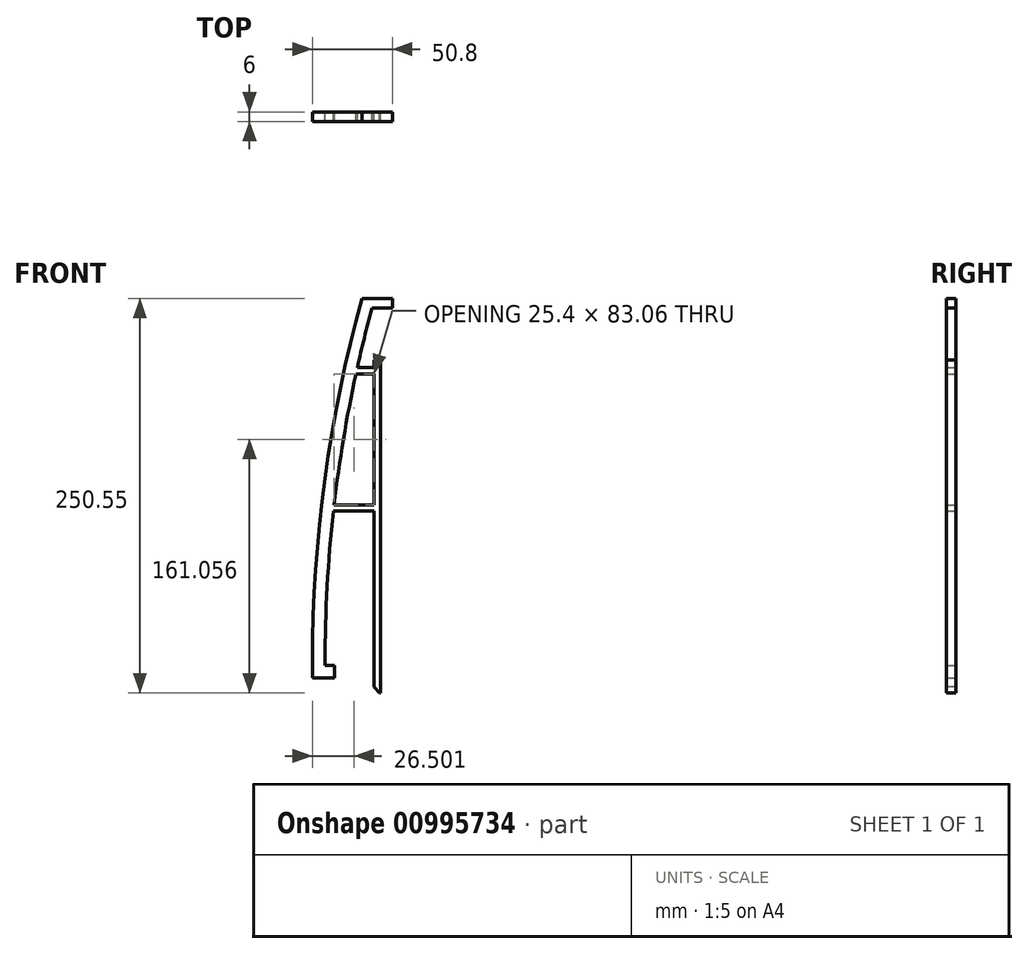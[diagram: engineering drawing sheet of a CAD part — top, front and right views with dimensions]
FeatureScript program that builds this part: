
annotation { "Feature Type Name" : "Feature", "Feature Type Description" : "" }
export const myFeature = defineFeature(function(context is Context, id is Id, definition is map)
    precondition{}
    {
        {
            var Q0;
            Q0=qCreatedBy(makeId("Front.planeOp"),FACE);
            var sketch = newSketch(context, id + "F0", { "sketchPlane" : qUnion([Q0])});
            skLineSegment(sketch, "E0", {"start": v(-4.2, 235) * mm, "end": v(-17.2, 235) * mm});
            skLineSegment(sketch, "E1", {"start": v(-4.2, 241) * mm, "end": v(-23.56, 241) * mm});
            skLineSegment(sketch, "E2", {"start": v(-47, 0) * mm, "end": v(-47, 10) * mm});
            skLineSegment(sketch, "E3", {"start": v(-55, 0) * mm, "end": v(-55, 10) * mm});
            skLineSegment(sketch, "E4", {"start": v(-47, 0) * mm, "end": v(-55, 0) * mm});
            skArc(sketch, "E5", {"start": v(-17.2, 235) * mm, "mid": v(-22.07, 216.07) * mm, "end": v(-26.52, 197.04) * mm});
            skArc(sketch, "E6", {"start": v(-23.56, 241) * mm, "mid": v(-47.1, 126.56) * mm, "end": v(-55, 10) * mm});
            skLineSegment(sketch, "E7", {"start": v(-4.2, 241) * mm, "end": v(-4.2, 235) * mm});
            skLineSegment(sketch, "E8", {"start": v(-11.8, -9.55) * mm, "end": v(-11.8, 197.04) * mm});
            skLineSegment(sketch, "E9", {"start": v(-15.8, 197.04) * mm, "end": v(-26.52, 197.04) * mm});
            skLineSegment(sketch, "E10", {"start": v(-27.4, 193.04) * mm, "end": v(-15.8, 193.04) * mm});
            skLineSegment(sketch, "E11", {"start": v(-15.8, 193.04) * mm, "end": v(-15.8, 109.97) * mm});
            skLineSegment(sketch, "E12", {"start": v(-15.8, -9.55) * mm, "end": v(-11.8, -9.55) * mm});
            skLineSegment(sketch, "E13", {"start": v(-15.8, 109.97) * mm, "end": v(-41.2, 109.97) * mm});
            skLineSegment(sketch, "E14", {"start": v(-15.8, 105.97) * mm, "end": v(-41.65, 105.97) * mm});
            skLineSegment(sketch, "E15", {"start": v(-15.8, 197.04) * mm, "end": v(-15.8, 202.04) * mm});
            skLineSegment(sketch, "E16", {"start": v(-15.8, 202.04) * mm, "end": v(-11.8, 202.04) * mm});
            skLineSegment(sketch, "E17", {"start": v(-11.8, 202.04) * mm, "end": v(-11.8, 197.04) * mm});
            skArc(sketch, "E18.trimOffspring", {"start": v(-27.4, 193.04) * mm, "mid": v(-35.3, 151.67) * mm, "end": v(-41.2, 109.97) * mm});
            skLineSegment(sketch, "E19.trimOffspring", {"start": v(-15.8, 105.97) * mm, "end": v(-15.8, -9.55) * mm});
            skArc(sketch, "E20.trimOffspring", {"start": v(-41.65, 105.97) * mm, "mid": v(-45.66, 58.06) * mm, "end": v(-47, 10) * mm});
            skSolve(sketch);
        }
        {
            var Q0;
            Q0=makeQuery(id+"F0.imprint","IMPRINT",FACE,{"disambiguationData":[TD([[makeQuery(id+"F0.imprint","IMPRINT",EDGE,{"derivedFrom":sQuery(id+"F0.wireOp",EDGE,"E0")}),-1.0]])]});
            extrude(context, id + "F1", {"entities" : qUnion([Q0]), "depth" : 6 * mm, "offsetDistance" : 25 * mm});
        }
        {
            var Q0;
            Q0=makeQuery(id+"F1.opExtrude","SWEPT_EDGE",EDGE,{"disambiguationData":[OSD([sQuery(id+"F0.wireOp",EDGE,"E12"),sQuery(id+"F0.wireOp",EDGE,"E19.trimOffspring")])]});
            chamfer(context, id + "F2", {"entities" : qUnion([Q0]), "chamferType" : ChamferType.TWO_OFFSETS, "width1" : 3.5 * mm, "oppositeDirection" : false, "width2" : 4 * mm, "tangentPropagation" : true});
        }
        {
            var Q0;
            Q0=makeQuery(id+"F1.opExtrude","SWEPT_FACE",FACE,{"disambiguationData":[OSD([sQuery(id+"F0.wireOp",EDGE,"E2")])]});
            extrude(context, id + "F3", {"entities" : qUnion([Q0]), "operationType" : NewBodyOperationType.ADD, "depth" : 6 * mm, "offsetDistance" : 25 * mm});
        }
        {
            var Q0;
            Q0=makeQuery(id+"F3.opExtrude","SWEPT_FACE",FACE,{"disambiguationData":[OSD([sQuery(id+"F0.wireOp",EDGE,"E2"),sQuery(id+"F0.wireOp",EDGE,"E20.trimOffspring")])]});
            extrude(context, id + "F4", {"entities" : qUnion([Q0]), "operationType" : NewBodyOperationType.REMOVE, "oppositeDirection" : true, "depth" : 2 * mm, "offsetDistance" : 25 * mm});
        }
    });
